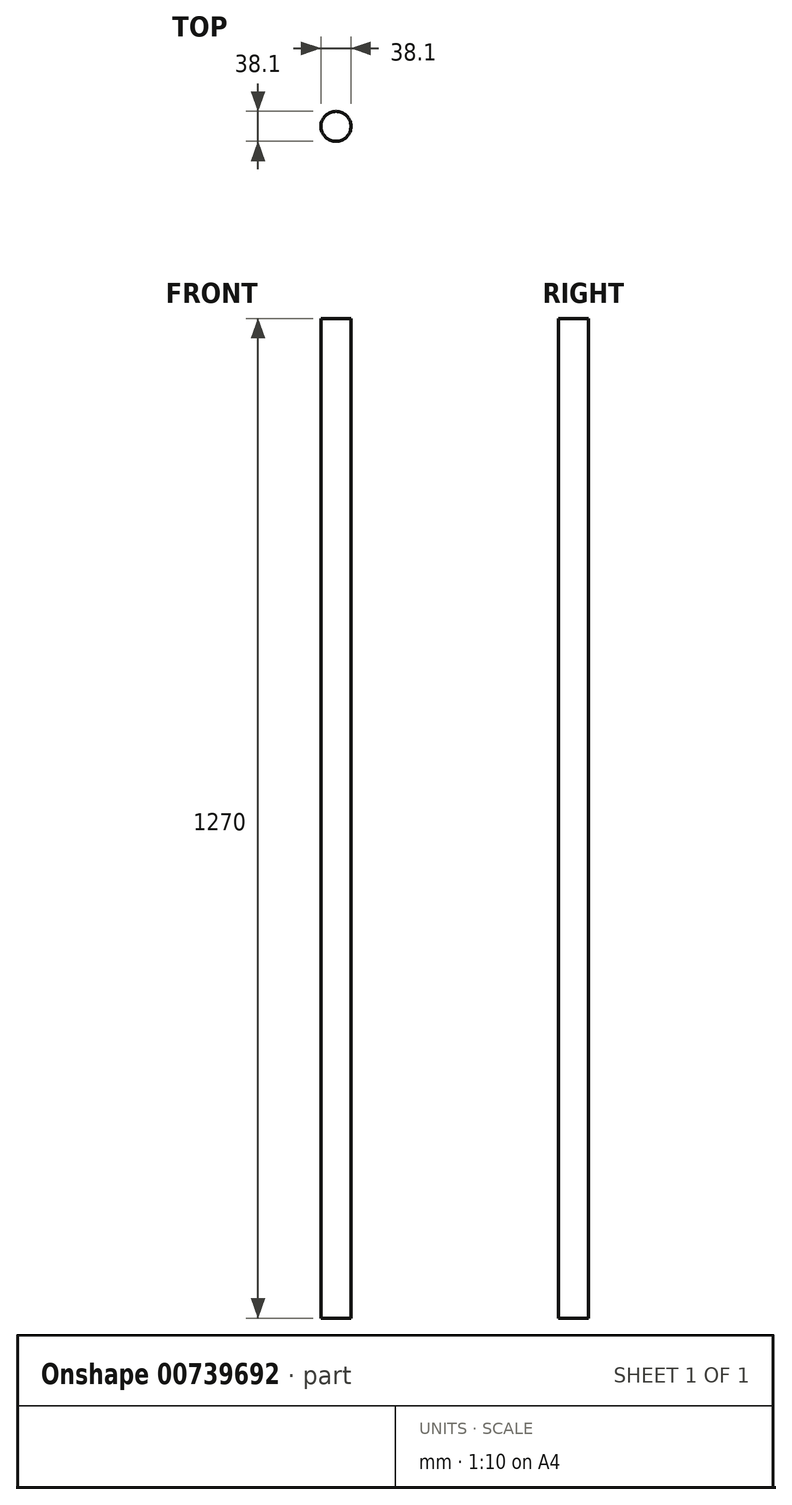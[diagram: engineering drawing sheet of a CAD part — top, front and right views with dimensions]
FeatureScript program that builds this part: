
annotation { "Feature Type Name" : "Feature", "Feature Type Description" : "" }
export const myFeature = defineFeature(function(context is Context, id is Id, definition is map)
    precondition{}
    {
        {
            var Q0;
            Q0=qCreatedBy(makeId("Top.planeOp"),FACE);
            var sketch = newSketch(context, id + "F0", { "sketchPlane" : qUnion([Q0])});
            skCircle(sketch, "E0", {"center": v(0, 0) * mm, "radius": 19.05 * mm});
            skSolve(sketch);
        }
        {
            var Q0;
            Q0=makeQuery(id+"F0.imprint","IMPRINT",FACE,{"disambiguationData":[TD([[makeQuery(id+"F0.imprint","IMPRINT",EDGE,{"derivedFrom":sQuery(id+"F0.wireOp",EDGE,"E0")}),1.0]])]});
            extrude(context, id + "F1", {"entities" : qUnion([Q0]), "depth" : 1270 * mm, "offsetDistance" : 25.4 * mm});
        }
    });
